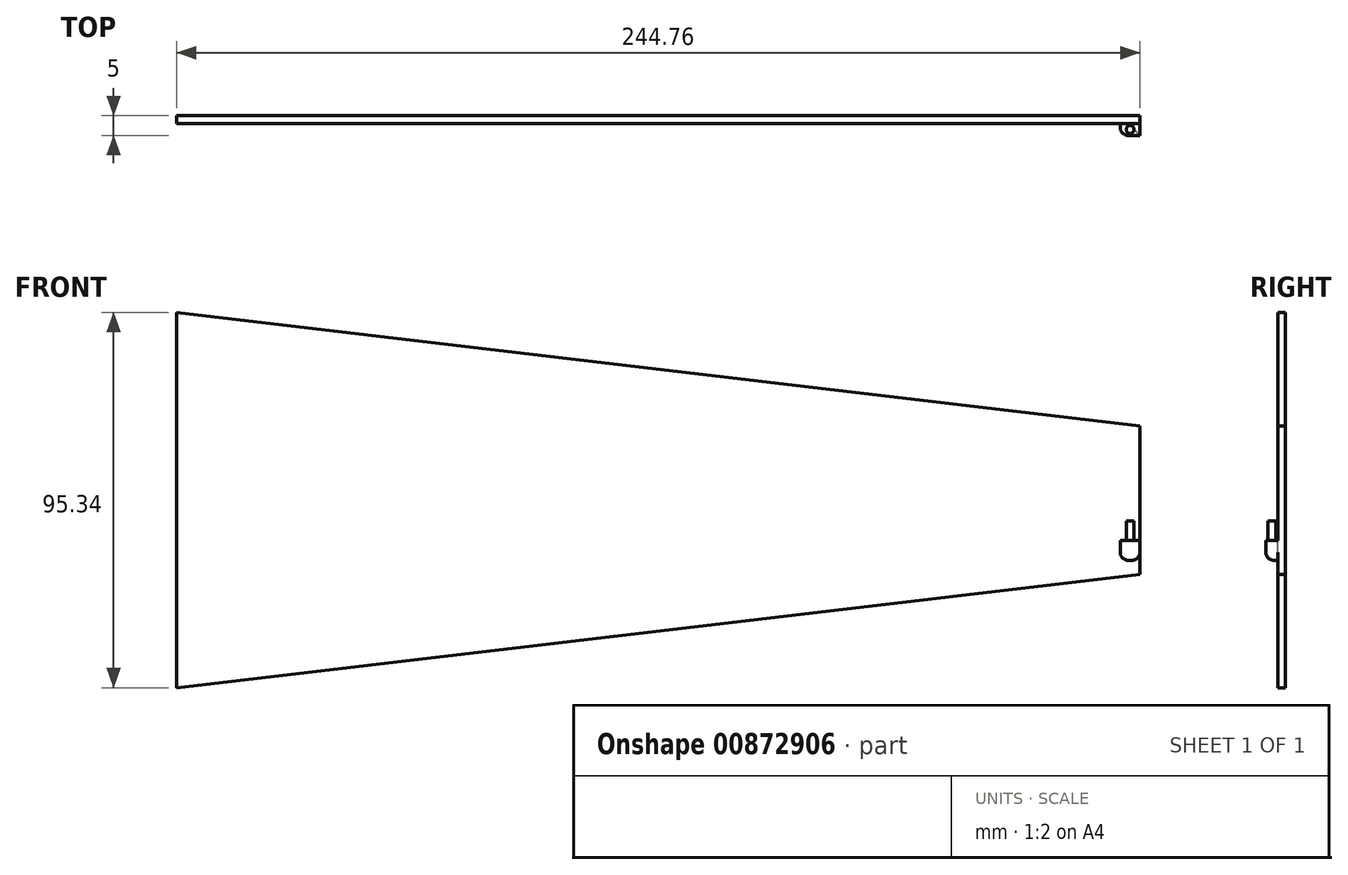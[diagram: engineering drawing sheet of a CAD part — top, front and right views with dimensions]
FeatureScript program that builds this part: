
annotation { "Feature Type Name" : "Feature", "Feature Type Description" : "" }
export const myFeature = defineFeature(function(context is Context, id is Id, definition is map)
    precondition{}
    {
        {
            var Q0;
            Q0=qCreatedBy(makeId("Front.planeOp"),FACE);
            var sketch = newSketch(context, id + "F0", { "sketchPlane" : qUnion([Q0])});
            skLineSegment(sketch, "E0.0", {"start": v(122.38, 18.87) * mm, "end": v(-122.38, 47.67) * mm});
            skLineSegment(sketch, "E0.1", {"start": v(122.38, -18.87) * mm, "end": v(122.38, 18.87) * mm});
            skLineSegment(sketch, "E0.2", {"start": v(-122.38, -47.67) * mm, "end": v(122.38, -18.87) * mm});
            skLineSegment(sketch, "E0.3", {"start": v(-122.38, 47.67) * mm, "end": v(-122.38, -47.67) * mm});
            skLineSegment(sketch, "E1.left", {"start": v(-122.38, 27.67) * mm, "end": v(-122.38, 22.67) * mm});
            skLineSegment(sketch, "E2.bottom", {"start": v(122.38, -15.29) * mm, "end": v(117.38, -15.29) * mm});
            skLineSegment(sketch, "E2.top", {"start": v(122.38, -10.29) * mm, "end": v(117.38, -10.29) * mm});
            skLineSegment(sketch, "E2.left", {"start": v(122.38, -15.29) * mm, "end": v(122.38, -10.29) * mm});
            skLineSegment(sketch, "E2.right", {"start": v(117.38, -15.29) * mm, "end": v(117.38, -10.29) * mm});
            skSolve(sketch);
        }
        {
            var Q0;
            Q0=makeQuery(id+"F0.imprint","IMPRINT",FACE,{"disambiguationData":[TD([[makeQuery(id+"F0.imprint","IMPRINT",EDGE,{"derivedFrom":sQuery(id+"F0.wireOp",EDGE,"E0.0")}),1.0]])]});
            extrude(context, id + "F1", {"entities" : qUnion([Q0]), "depth" : 2 * mm, "offsetDistance" : 25 * mm});
        }
        {
            var Q0;
            Q0=makeQuery(id+"F0.imprint","IMPRINT",FACE,{"disambiguationData":[TD([[makeQuery(id+"F0.imprint","IMPRINT",EDGE,{"derivedFrom":sQuery(id+"F0.wireOp",EDGE,"E2.bottom")}),-1.0]])]});
            extrude(context, id + "F2", {"entities" : qUnion([Q0]), "operationType" : NewBodyOperationType.ADD, "depth" : 5 * mm, "offsetDistance" : 25 * mm});
        }
        {
            var Q0;
            Q0=makeQuery(id+"F2.opExtrude","SWEPT_FACE",FACE,{"disambiguationData":[OSD([sQuery(id+"F0.wireOp",EDGE,"E2.top")])]});
            var sketch = newSketch(context, id + "F3", { "sketchPlane" : qUnion([Q0])});
            skPoint(sketch, "E3", {"position": v(119.88, -3.5) * mm});
            skCircle(sketch, "E4", {"center": v(119.88, -3.5) * mm, "radius": 1 * mm});
            skSolve(sketch);
        }
        {
            var Q0;
            Q0=makeQuery(id+"F3.imprint","IMPRINT",FACE,{"disambiguationData":[TD([[makeQuery(id+"F3.imprint","IMPRINT",EDGE,{"derivedFrom":sQuery(id+"F3.wireOp",EDGE,"E4")}),1.0]])]});
            extrude(context, id + "F4", {"entities" : qUnion([Q0]), "operationType" : NewBodyOperationType.ADD, "depth" : 5 * mm, "offsetDistance" : 25 * mm});
        }
        {
            var Q0;
            Q0=makeQuery(id+"F2.opExtrude","CAP_EDGE",EDGE,{"disambiguationData":[OSD([sQuery(id+"F0.wireOp",EDGE,"E2.bottom")])],"isStart":false});
            var Q1;
            Q1=makeQuery(id+"F2.opExtrude","CAP_EDGE",EDGE,{"disambiguationData":[OSD([sQuery(id+"F0.wireOp",EDGE,"E2.left")])],"isStart":false});
            var Q2;
            Q2=makeQuery(id+"F2.opExtrude","SWEPT_EDGE",EDGE,{"disambiguationData":[OSD([sQuery(id+"F0.wireOp",EDGE,"E0.1"),sQuery(id+"F0.wireOp",EDGE,"E2.bottom"),sQuery(id+"F0.wireOp",EDGE,"E2.left")])]});
            var Q3;
            Q3=makeQuery(id+"F2.opExtrude","SWEPT_EDGE",EDGE,{"disambiguationData":[OSD([sQuery(id+"F0.wireOp",EDGE,"E2.bottom"),sQuery(id+"F0.wireOp",EDGE,"E2.right")])]});
            var Q4;
            Q4=makeQuery(id+"F2.opExtrude","CAP_EDGE",EDGE,{"disambiguationData":[OSD([sQuery(id+"F0.wireOp",EDGE,"E2.right")])],"isStart":false});
            fillet(context, id + "F5", {"entities" : qUnion([Q0, Q1, Q2, Q3, Q4]), "radius" : 2 * mm, "tangentPropagation" : true, "allowEdgeOverflow" : false});
        }
    });
